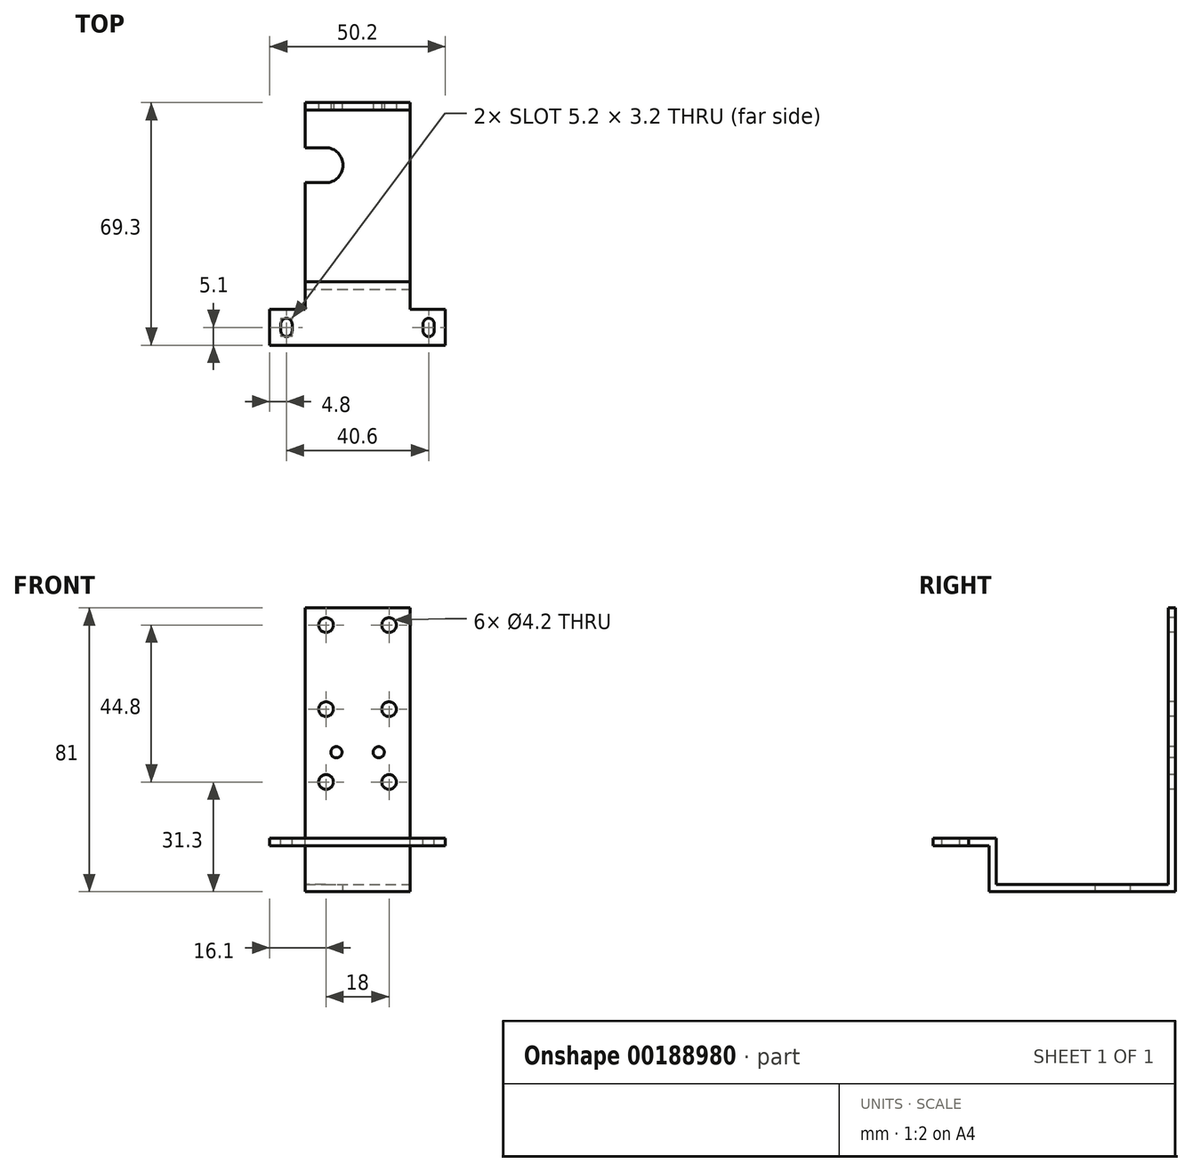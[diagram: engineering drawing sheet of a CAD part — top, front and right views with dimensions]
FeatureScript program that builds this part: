
annotation { "Feature Type Name" : "Feature", "Feature Type Description" : "" }
export const myFeature = defineFeature(function(context is Context, id is Id, definition is map)
    precondition{}
    {
        {
            var Q0;
            Q0=qCreatedBy(makeId("Front.planeOp"),FACE);
            var sketch = newSketch(context, id + "F0", { "sketchPlane" : qUnion([Q0])});
            skLineSegment(sketch, "E0.bottom", {"start": v(15, -40.5) * mm, "end": v(-15, -40.5) * mm});
            skLineSegment(sketch, "E0.top", {"start": v(15, 40.5) * mm, "end": v(-15, 40.5) * mm});
            skLineSegment(sketch, "E0.left", {"start": v(15, -40.5) * mm, "end": v(15, 40.5) * mm});
            skLineSegment(sketch, "E0.right", {"start": v(-15, -40.5) * mm, "end": v(-15, 40.5) * mm});
            skPoint(sketch, "E0.middle", {"position": v(0, 0) * mm});
            skSolve(sketch);
        }
        {
            var Q0;
            Q0=qSketchRegion(id+"F0",true);
            extrude(context, id + "F1", {"entities" : qUnion([Q0]), "depth" : 2.1 * mm});
        }
        {
            var Q0;
            Q0=makeQuery(id+"F1.opExtrude","CAP_FACE",FACE,{"disambiguationData":[OSD([sQuery(id+"F0.wireOp",EDGE,"E0.bottom"),sQuery(id+"F0.wireOp",EDGE,"E0.top"),sQuery(id+"F0.wireOp",EDGE,"E0.left"),sQuery(id+"F0.wireOp",EDGE,"E0.right")])],"isStart":false});
            var sketch = newSketch(context, id + "F2", { "sketchPlane" : qUnion([Q0])});
            skLineSegment(sketch, "E1.bottom", {"start": v(-15, -40.5) * mm, "end": v(15, -40.5) * mm});
            skLineSegment(sketch, "E1.top", {"start": v(-15, -38.4) * mm, "end": v(15, -38.4) * mm});
            skLineSegment(sketch, "E1.left", {"start": v(-15, -40.5) * mm, "end": v(-15, -38.4) * mm});
            skLineSegment(sketch, "E1.right", {"start": v(15, -40.5) * mm, "end": v(15, -38.4) * mm});
            skSolve(sketch);
        }
        {
            var Q0;
            Q0=qSketchRegion(id+"F2",true);
            extrude(context, id + "F3", {"entities" : qUnion([Q0]), "operationType" : NewBodyOperationType.ADD, "depth" : 51.2 * mm});
        }
        {
            var Q0;
            Q0=makeQuery(id+"F3.opExtrude","SWEPT_FACE",FACE,{"disambiguationData":[OSD([sQuery(id+"F2.wireOp",EDGE,"E1.top")])]});
            var sketch = newSketch(context, id + "F4", { "sketchPlane" : qUnion([Q0])});
            skLineSegment(sketch, "E2.bottom", {"start": v(-15, -53.3) * mm, "end": v(15, -53.3) * mm});
            skLineSegment(sketch, "E2.top", {"start": v(-15, -51.2) * mm, "end": v(15, -51.2) * mm});
            skLineSegment(sketch, "E2.left", {"start": v(-15, -53.3) * mm, "end": v(-15, -51.2) * mm});
            skLineSegment(sketch, "E2.right", {"start": v(15, -53.3) * mm, "end": v(15, -51.2) * mm});
            skSolve(sketch);
        }
        {
            var Q0;
            Q0=qSketchRegion(id+"F4",true);
            extrude(context, id + "F5", {"entities" : qUnion([Q0]), "operationType" : NewBodyOperationType.ADD, "depth" : 13.1 * mm});
        }
        {
            var Q0;
            Q0=makeQuery(id+"F5.boolean.opBoolean","MERGE",FACE,{"derivedFrom":[makeQuery(id+"F3.opExtrude","CAP_FACE",FACE,{"disambiguationData":[OSD([sQuery(id+"F2.wireOp",EDGE,"E1.bottom"),sQuery(id+"F2.wireOp",EDGE,"E1.top"),sQuery(id+"F2.wireOp",EDGE,"E1.left"),sQuery(id+"F2.wireOp",EDGE,"E1.right")])],"isStart":false}),makeQuery(id+"F5.opExtrude","SWEPT_FACE",FACE,{"disambiguationData":[OSD([sQuery(id+"F4.wireOp",EDGE,"E2.bottom")])]})]});
            var sketch = newSketch(context, id + "F6", { "sketchPlane" : qUnion([Q0])});
            skLineSegment(sketch, "E3.bottom", {"start": v(-15, -25.3) * mm, "end": v(15, -25.3) * mm});
            skLineSegment(sketch, "E3.top", {"start": v(-15, -27.4) * mm, "end": v(15, -27.4) * mm});
            skLineSegment(sketch, "E3.left", {"start": v(-15, -25.3) * mm, "end": v(-15, -27.4) * mm});
            skLineSegment(sketch, "E3.right", {"start": v(15, -25.3) * mm, "end": v(15, -27.4) * mm});
            skSolve(sketch);
        }
        {
            var Q0;
            Q0=qSketchRegion(id+"F6",true);
            extrude(context, id + "F7", {"entities" : qUnion([Q0]), "operationType" : NewBodyOperationType.ADD, "depth" : 16 * mm});
        }
        {
            var Q0;
            Q0=makeQuery(id+"F7.boolean.opBoolean","MERGE",FACE,{"derivedFrom":[makeQuery(id+"F5.opExtrude","CAP_FACE",FACE,{"disambiguationData":[OSD([sQuery(id+"F4.wireOp",EDGE,"E2.bottom"),sQuery(id+"F4.wireOp",EDGE,"E2.top"),sQuery(id+"F4.wireOp",EDGE,"E2.left"),sQuery(id+"F4.wireOp",EDGE,"E2.right")])],"isStart":false}),makeQuery(id+"F7.opExtrude","SWEPT_FACE",FACE,{"disambiguationData":[OSD([sQuery(id+"F6.wireOp",EDGE,"E3.bottom")])]})]});
            var sketch = newSketch(context, id + "F8", { "sketchPlane" : qUnion([Q0])});
            skLineSegment(sketch, "E4.bottom", {"start": v(-25.1, -69.3) * mm, "end": v(25.1, -69.3) * mm});
            skLineSegment(sketch, "E4.top", {"start": v(-25.1, -59.1) * mm, "end": v(25.1, -59.1) * mm});
            skLineSegment(sketch, "E4.left", {"start": v(-25.1, -69.3) * mm, "end": v(-25.1, -59.1) * mm});
            skLineSegment(sketch, "E4.right", {"start": v(25.1, -69.3) * mm, "end": v(25.1, -59.1) * mm});
            skLineSegment(sketch, "E5", {"start": v(0, -51.2) * mm, "end": v(0, -65.26) * mm});
            skSolve(sketch);
        }
        {
            var Q0;
            {var subQ3=sQuery(id+"F8.wireOp",EDGE,"E4.left");Q0=makeQuery(id+"F8.imprint","IMPRINT",FACE,{"disambiguationData":[TD([[makeQuery(id+"F8.imprint","IMPRINT",EDGE,{"derivedFrom":subQ3}),-1.0]])]});}
            var Q1;
            {var subQ3=sQuery(id+"F8.wireOp",EDGE,"E4.right");Q1=makeQuery(id+"F8.imprint","IMPRINT",FACE,{"disambiguationData":[TD([[makeQuery(id+"F8.imprint","IMPRINT",EDGE,{"derivedFrom":subQ3}),1.0]])]});}
            extrude(context, id + "F9", {"entities" : qUnion([Q0, Q1]), "operationType" : NewBodyOperationType.ADD, "oppositeDirection" : true, "depth" : 2.1 * mm});
        }
        {
            var Q0;
            {var subQ0=sQuery(id+"F8.wireOp",EDGE,"E4.top");var subQ1=sQuery(id+"F8.wireOp",EDGE,"E4.bottom");var subQ2=sQuery(id+"F6.wireOp",EDGE,"E3.bottom");var subQ3=sQuery(id+"F4.wireOp",EDGE,"E2.right");var subQ4=sQuery(id+"F4.wireOp",EDGE,"E2.left");Q0=makeQuery(id+"F9.boolean.opBoolean","MERGE",FACE,{"derivedFrom":[makeQuery(id+"F7.boolean.opBoolean","MERGE",FACE,{"derivedFrom":[makeQuery(id+"F5.opExtrude","CAP_FACE",FACE,{"disambiguationData":[OSD([sQuery(id+"F4.wireOp",EDGE,"E2.bottom"),sQuery(id+"F4.wireOp",EDGE,"E2.top"),subQ4,subQ3])],"isStart":false}),makeQuery(id+"F7.opExtrude","SWEPT_FACE",FACE,{"disambiguationData":[OSD([subQ2])]})]}),makeQuery(id+"F9.opExtrude","CAP_FACE",FACE,{"disambiguationData":[OSD([subQ4,subQ2,sQuery(id+"F6.wireOp",EDGE,"E3.left"),subQ1,subQ0,sQuery(id+"F8.wireOp",EDGE,"E4.left")])],"isStart":true}),makeQuery(id+"F9.opExtrude","CAP_FACE",FACE,{"disambiguationData":[OSD([subQ3,subQ2,sQuery(id+"F6.wireOp",EDGE,"E3.right"),subQ1,subQ0,sQuery(id+"F8.wireOp",EDGE,"E4.right")])],"isStart":true})]});}
            var sketch = newSketch(context, id + "F10", { "sketchPlane" : qUnion([Q0])});
            skArc(sketch, "E6", {"start": v(-21.9, -65.2) * mm, "mid": v(-20.3, -66.8) * mm, "end": v(-18.7, -65.2) * mm});
            skArc(sketch, "E7", {"start": v(-18.7, -63.2) * mm, "mid": v(-20.3, -61.6) * mm, "end": v(-21.9, -63.2) * mm});
            skLineSegment(sketch, "E8", {"start": v(-21.9, -63.2) * mm, "end": v(-21.9, -65.2) * mm});
            skLineSegment(sketch, "E9", {"start": v(-18.7, -65.2) * mm, "end": v(-18.7, -63.2) * mm});
            skLineSegment(sketch, "E10", {"start": v(-20.3, -63.2) * mm, "end": v(-20.3, -65.2) * mm});
            skPoint(sketch, "E11", {"position": v(-20.3, -64.2) * mm});
            skLineSegment(sketch, "E12", {"start": v(0, -69.3) * mm, "end": v(0, -51.2) * mm});
            skLineSegment(sketch, "E13.MirrorCS", {"start": v(18.7, -65.2) * mm, "end": v(18.7, -63.2) * mm});
            skArc(sketch, "E14.MirrorCS", {"start": v(18.7, -63.2) * mm, "mid": v(20.3, -61.6) * mm, "end": v(21.9, -63.2) * mm});
            skLineSegment(sketch, "E15.MirrorCS", {"start": v(21.9, -63.2) * mm, "end": v(21.9, -65.2) * mm});
            skArc(sketch, "E16.MirrorCS", {"start": v(21.9, -65.2) * mm, "mid": v(20.3, -66.8) * mm, "end": v(18.7, -65.2) * mm});
            skSolve(sketch);
        }
        {
            var Q0;
            Q0=makeQuery(id+"F10.imprint","IMPRINT",FACE,{"disambiguationData":[TD([[makeQuery(id+"F10.imprint","IMPRINT",EDGE,{"derivedFrom":sQuery(id+"F10.wireOp",EDGE,"E6")}),1.0]])]});
            var Q1;
            Q1=makeQuery(id+"F10.imprint","IMPRINT",FACE,{"disambiguationData":[TD([[makeQuery(id+"F10.imprint","IMPRINT",EDGE,{"derivedFrom":sQuery(id+"F10.wireOp",EDGE,"E13.MirrorCS")}),-1.0]])]});
            extrude(context, id + "F11", {"entities" : qUnion([Q0, Q1]), "operationType" : NewBodyOperationType.REMOVE, "endBound" : BoundingType.THROUGH_ALL, "oppositeDirection" : true, "depth" : 25 * mm});
        }
        {
            var Q0;
            Q0=makeQuery(id+"F3.opExtrude","SWEPT_FACE",FACE,{"disambiguationData":[OSD([sQuery(id+"F2.wireOp",EDGE,"E1.top")])]});
            var sketch = newSketch(context, id + "F12", { "sketchPlane" : qUnion([Q0])});
            skArc(sketch, "E17", {"start": v(-9.15, -22.9) * mm, "mid": v(-4.15, -17.9) * mm, "end": v(-9.15, -12.9) * mm});
            skLineSegment(sketch, "E18", {"start": v(-9.15, -12.9) * mm, "end": v(-15, -12.9) * mm});
            skLineSegment(sketch, "E19", {"start": v(-9.15, -22.9) * mm, "end": v(-15, -22.9) * mm});
            skLineSegment(sketch, "E20", {"start": v(-15, -22.9) * mm, "end": v(-15, -12.9) * mm});
            skSolve(sketch);
        }
        {
            var Q0;
            Q0=qSketchRegion(id+"F12",true);
            extrude(context, id + "F13", {"entities" : qUnion([Q0]), "operationType" : NewBodyOperationType.REMOVE, "endBound" : BoundingType.THROUGH_ALL, "oppositeDirection" : true, "depth" : 25 * mm});
        }
        {
            var Q0;
            Q0=makeQuery(id+"F1.opExtrude","CAP_FACE",FACE,{"disambiguationData":[OSD([sQuery(id+"F0.wireOp",EDGE,"E0.bottom"),sQuery(id+"F0.wireOp",EDGE,"E0.top"),sQuery(id+"F0.wireOp",EDGE,"E0.left"),sQuery(id+"F0.wireOp",EDGE,"E0.right")])],"isStart":false});
            var sketch = newSketch(context, id + "F14", { "sketchPlane" : qUnion([Q0])});
            skCircle(sketch, "E21", {"center": v(9, 35.6) * mm, "radius": 2.1 * mm});
            skCircle(sketch, "E22.0.1.0", {"center": v(9, 11.6) * mm, "radius": 2.1 * mm});
            skCircle(sketch, "E22.1.0.0", {"center": v(-9, 35.6) * mm, "radius": 2.1 * mm});
            skCircle(sketch, "E22.1.1.0", {"center": v(-9, 11.6) * mm, "radius": 2.1 * mm});
            skLineSegment(sketch, "E22.direction1", {"start": v(9, 35.6) * mm, "end": v(-9, 35.6) * mm, "construction": true});
            skLineSegment(sketch, "E22.direction2", {"start": v(9, 35.6) * mm, "end": v(9, 11.6) * mm, "construction": true});
            skCircle(sketch, "E23", {"center": v(9, -9.2) * mm, "radius": 2.1 * mm});
            skCircle(sketch, "E24.1.0.0", {"center": v(-9, -9.2) * mm, "radius": 2.1 * mm});
            skLineSegment(sketch, "E24.direction1", {"start": v(9, -9.2) * mm, "end": v(-9, -9.2) * mm, "construction": true});
            skCircle(sketch, "E25", {"center": v(6.05, -0.7) * mm, "radius": 1.6 * mm});
            skCircle(sketch, "E26", {"center": v(-6.05, -0.7) * mm, "radius": 1.6 * mm});
            skSolve(sketch);
        }
        {
            var Q0;
            Q0=qSketchRegion(id+"F14",true);
            extrude(context, id + "F15", {"entities" : qUnion([Q0]), "operationType" : NewBodyOperationType.REMOVE, "endBound" : BoundingType.THROUGH_ALL, "oppositeDirection" : true, "depth" : 25 * mm});
        }
    });
